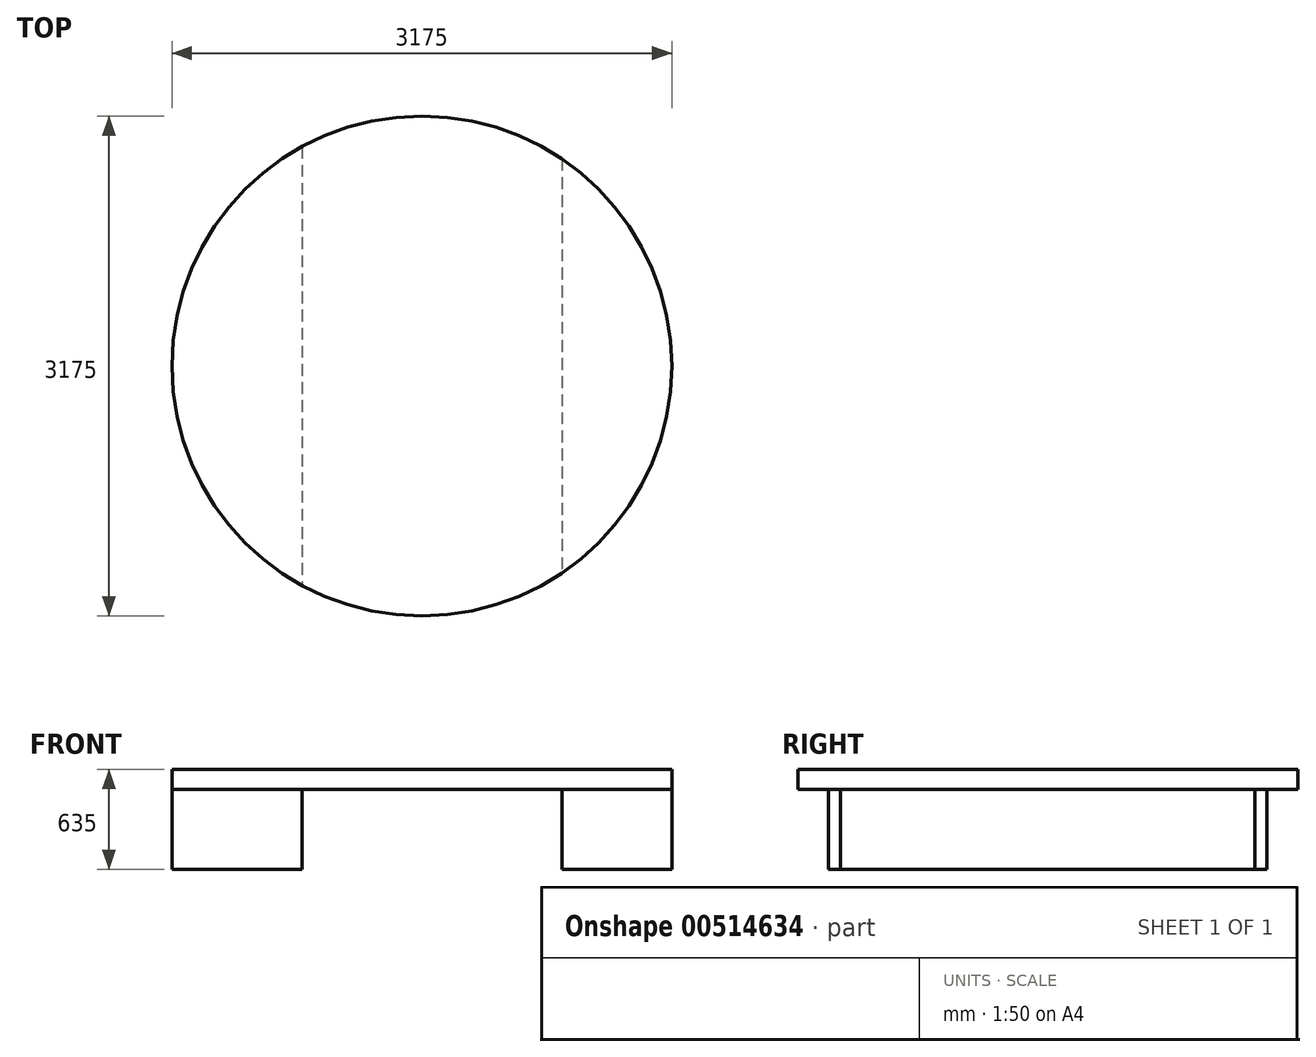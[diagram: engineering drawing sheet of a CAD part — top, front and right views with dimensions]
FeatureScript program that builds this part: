
annotation { "Feature Type Name" : "Feature", "Feature Type Description" : "" }
export const myFeature = defineFeature(function(context is Context, id is Id, definition is map)
    precondition{}
    {
        {
            var Q0;
            Q0=qCreatedBy(makeId("Top.planeOp"),FACE);
            var sketch = newSketch(context, id + "F0", { "sketchPlane" : qUnion([Q0])});
            skCircle(sketch, "E0", {"center": v(0, 0) * mm, "radius": 1587.5 * mm});
            skLineSegment(sketch, "E1.bottom", {"start": v(-762, 1854.86) * mm, "end": v(889, 1854.86) * mm});
            skLineSegment(sketch, "E1.top", {"start": v(-762, -2790) * mm, "end": v(889, -2790) * mm});
            skLineSegment(sketch, "E1.left", {"start": v(-762, 1854.86) * mm, "end": v(-762, -2790) * mm});
            skLineSegment(sketch, "E1.right", {"start": v(889, 1854.86) * mm, "end": v(889, -2790) * mm});
            skSolve(sketch);
        }
        {
            var Q0;
            {var subQ0=sQuery(id+"F0.wireOp",EDGE,"E1.left");var subQ1=sQuery(id+"F0.wireOp",EDGE,"E0");var subQ2=makeQuery(id+"F0.imprint","INTERSECT",VERTEX,{"disambiguationData":[OD(0.0)],"derivedFrom":[subQ1,subQ0]});Q0=makeQuery(id+"F0.imprint","IMPRINT",FACE,{"disambiguationData":[TD([[makeQuery(id+"F0.imprint","IMPRINT",EDGE,{"disambiguationData":[TD([[subQ2,-1.0]])],"derivedFrom":subQ1}),1.0]])]});}
            var Q1;
            {var subQ0=sQuery(id+"F0.wireOp",EDGE,"E1.right");var subQ1=sQuery(id+"F0.wireOp",EDGE,"E0");var subQ2=makeQuery(id+"F0.imprint","INTERSECT",VERTEX,{"disambiguationData":[OD(0.0)],"derivedFrom":[subQ1,subQ0]});Q1=makeQuery(id+"F0.imprint","IMPRINT",FACE,{"disambiguationData":[TD([[makeQuery(id+"F0.imprint","IMPRINT",EDGE,{"disambiguationData":[TD([[subQ2,1.0]])],"derivedFrom":subQ1}),1.0]])]});}
            extrude(context, id + "F1", {"entities" : qUnion([Q0, Q1]), "depth" : 508 * mm, "offsetDistance" : 25.4 * mm});
        }
        {
            var Q0;
            {var subQ0=sQuery(id+"F0.wireOp",EDGE,"E1.left");var subQ1=sQuery(id+"F0.wireOp",EDGE,"E0");Q0=makeQuery(id+"F1.opExtrude","CAP_VERTEX",VERTEX,{"disambiguationData":[OSD([subQ1,subQ0]),TDD([makeQuery(id+"F0.imprint","INTERSECT",VERTEX,{"disambiguationData":[OD(0.0)],"derivedFrom":[subQ1,subQ0]})])],"isStart":false});}
            var Q1;
            {var subQ0=sQuery(id+"F0.wireOp",EDGE,"E1.right");var subQ1=sQuery(id+"F0.wireOp",EDGE,"E0");Q1=makeQuery(id+"F1.opExtrude","CAP_VERTEX",VERTEX,{"disambiguationData":[OSD([subQ1,subQ0]),TDD([makeQuery(id+"F0.imprint","INTERSECT",VERTEX,{"disambiguationData":[OD(1.0)],"derivedFrom":[subQ1,subQ0]})])],"isStart":false});}
            var Q2;
            {var subQ0=sQuery(id+"F0.wireOp",EDGE,"E1.left");var subQ1=sQuery(id+"F0.wireOp",EDGE,"E0");Q2=makeQuery(id+"F1.opExtrude","CAP_VERTEX",VERTEX,{"disambiguationData":[OSD([subQ1,subQ0]),TDD([makeQuery(id+"F0.imprint","INTERSECT",VERTEX,{"disambiguationData":[OD(1.0)],"derivedFrom":[subQ1,subQ0]})])],"isStart":false});}
            cPlane(context, id + "F2", {"entities" : qUnion([Q0, Q1, Q2]), "cplaneType" : CPlaneType.THREE_POINT, "offset" : 25.4 * mm, "width" : 152.4 * mm, "height" : 152.4 * mm});
        }
        {
            var Q0;
            Q0=qCreatedBy(id+"F2.planeOp",FACE);
            var sketch = newSketch(context, id + "F3", { "sketchPlane" : qUnion([Q0])});
            skCircle(sketch, "E2", {"center": v(0, 0) * mm, "radius": 1587.5 * mm});
            skSolve(sketch);
        }
        {
            var Q0;
            Q0=makeQuery(id+"F3.imprint","IMPRINT",FACE,{"disambiguationData":[TD([[makeQuery(id+"F3.imprint","IMPRINT",EDGE,{"derivedFrom":sQuery(id+"F3.wireOp",EDGE,"E2")}),1.0]])]});
            extrude(context, id + "F4", {"entities" : qUnion([Q0]), "depth" : 127 * mm, "offsetDistance" : 25.4 * mm});
        }
    });
